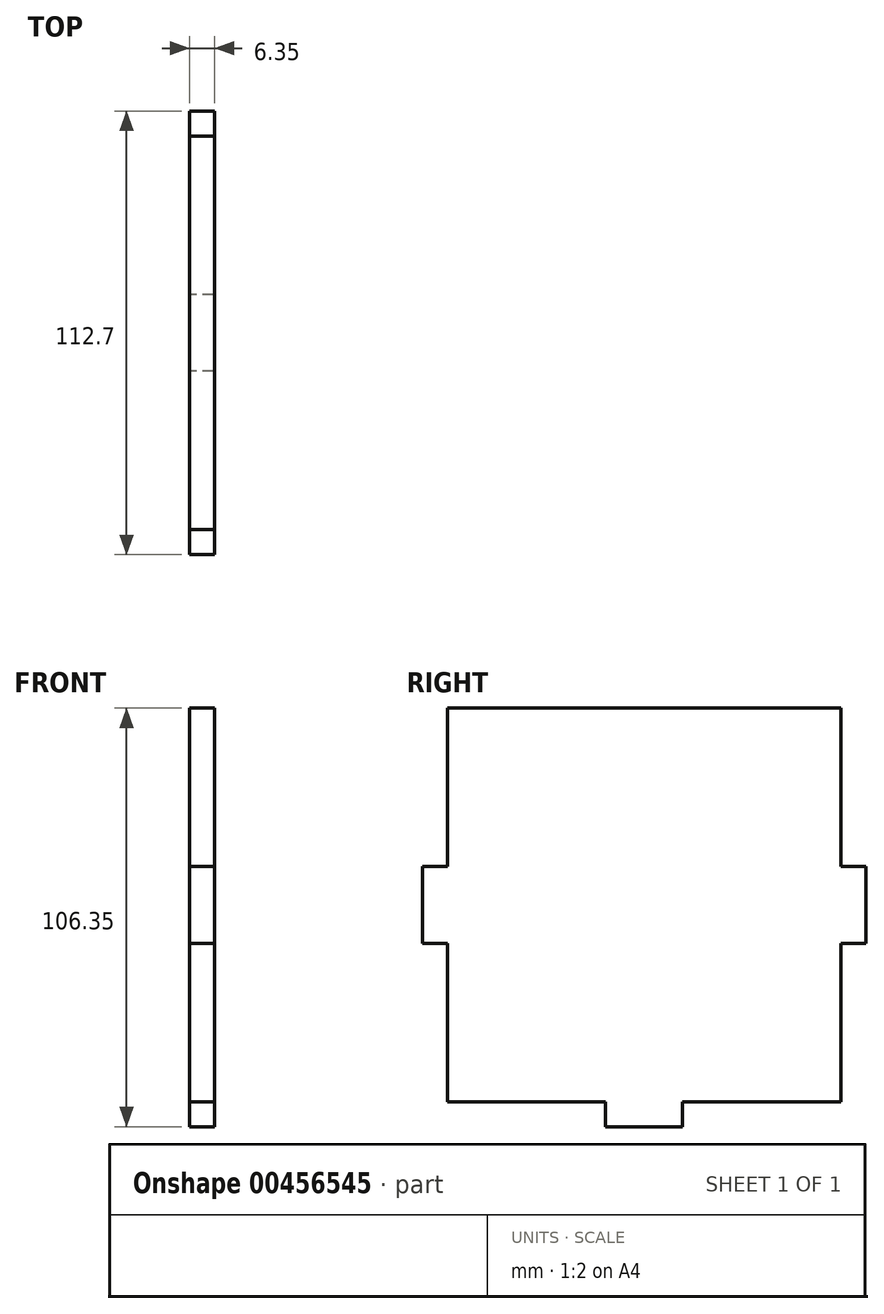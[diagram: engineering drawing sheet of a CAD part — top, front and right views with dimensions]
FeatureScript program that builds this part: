
annotation { "Feature Type Name" : "Feature", "Feature Type Description" : "" }
export const myFeature = defineFeature(function(context is Context, id is Id, definition is map)
    precondition{}
    {
        {
            var Q0;
            Q0=qCreatedBy(makeId("Right.planeOp"),FACE);
            var sketch = newSketch(context, id + "F0", { "sketchPlane" : qUnion([Q0])});
            skLineSegment(sketch, "E0.bottom", {"start": v(50, 50) * mm, "end": v(-50, 50) * mm});
            skLineSegment(sketch, "E0.top", {"start": v(50, -50) * mm, "end": v(-50, -50) * mm});
            skLineSegment(sketch, "E0.left", {"start": v(50, 50) * mm, "end": v(50, -50) * mm});
            skLineSegment(sketch, "E0.right", {"start": v(-50, 50) * mm, "end": v(-50, -50) * mm});
            skPoint(sketch, "E0.middle", {"position": v(0, 0) * mm});
            skLineSegment(sketch, "E1.bottom", {"start": v(-9.75, -50) * mm, "end": v(9.75, -50) * mm});
            skLineSegment(sketch, "E1.top", {"start": v(-9.75, -56.35) * mm, "end": v(9.75, -56.35) * mm});
            skLineSegment(sketch, "E1.left", {"start": v(-9.75, -50) * mm, "end": v(-9.75, -56.35) * mm});
            skLineSegment(sketch, "E1.right", {"start": v(9.75, -50) * mm, "end": v(9.75, -56.35) * mm});
            skLineSegment(sketch, "E2.bottom", {"start": v(-50, 9.75) * mm, "end": v(-56.35, 9.75) * mm});
            skLineSegment(sketch, "E2.top", {"start": v(-50, -9.75) * mm, "end": v(-56.35, -9.75) * mm});
            skLineSegment(sketch, "E2.left", {"start": v(-50, 9.75) * mm, "end": v(-50, -9.75) * mm});
            skLineSegment(sketch, "E2.right", {"start": v(-56.35, 9.75) * mm, "end": v(-56.35, -9.75) * mm});
            skLineSegment(sketch, "E3.bottom", {"start": v(50, 9.75) * mm, "end": v(56.35, 9.75) * mm});
            skLineSegment(sketch, "E3.top", {"start": v(50, -9.75) * mm, "end": v(56.35, -9.75) * mm});
            skLineSegment(sketch, "E3.left", {"start": v(50, 9.75) * mm, "end": v(50, -9.75) * mm});
            skLineSegment(sketch, "E3.right", {"start": v(56.35, 9.75) * mm, "end": v(56.35, -9.75) * mm});
            skSolve(sketch);
        }
        {
            var Q0;
            Q0 = qSketchRegion(id + "F0", true);
            extrude(context, id + "F1", {"entities" : qUnion([Q0]), "depth" : 6.35 * mm});
        }
    });
